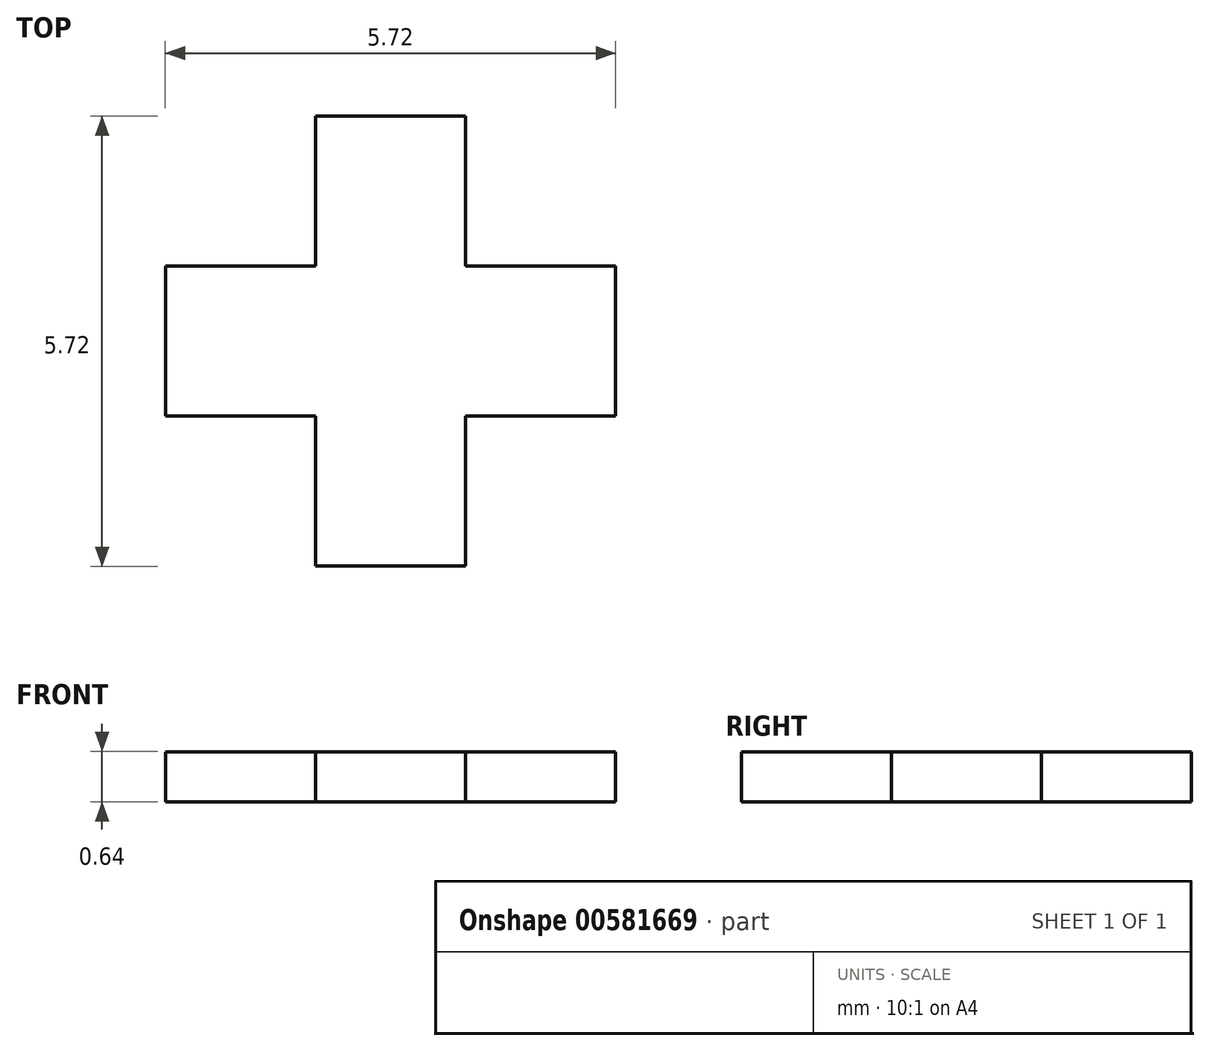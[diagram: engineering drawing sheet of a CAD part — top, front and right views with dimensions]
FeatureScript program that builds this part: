
annotation { "Feature Type Name" : "Feature", "Feature Type Description" : "" }
export const myFeature = defineFeature(function(context is Context, id is Id, definition is map)
    precondition{}
    {
        {
            var Q0;
            Q0=qCreatedBy(makeId("Top.planeOp"),FACE);
            var sketch = newSketch(context, id + "F0", { "sketchPlane" : qUnion([Q0])});
            skLineSegment(sketch, "E0", {"start": v(-33.75, -11.5) * mm, "end": v(-35.65, -11.5) * mm});
            skLineSegment(sketch, "E1", {"start": v(-35.65, -11.5) * mm, "end": v(-35.65, -13.4) * mm});
            skLineSegment(sketch, "E2", {"start": v(-35.65, -13.4) * mm, "end": v(-37.56, -13.4) * mm});
            skLineSegment(sketch, "E3", {"start": v(-37.56, -13.4) * mm, "end": v(-37.56, -15.3) * mm});
            skLineSegment(sketch, "E4", {"start": v(-37.56, -15.3) * mm, "end": v(-35.65, -15.3) * mm});
            skLineSegment(sketch, "E5", {"start": v(-35.65, -15.3) * mm, "end": v(-35.65, -17.2) * mm});
            skLineSegment(sketch, "E6", {"start": v(-35.65, -17.2) * mm, "end": v(-33.75, -17.2) * mm});
            skLineSegment(sketch, "E7", {"start": v(-33.75, -17.2) * mm, "end": v(-33.75, -15.3) * mm});
            skLineSegment(sketch, "E8", {"start": v(-33.75, -15.3) * mm, "end": v(-31.84, -15.3) * mm});
            skLineSegment(sketch, "E9", {"start": v(-31.84, -15.3) * mm, "end": v(-31.84, -13.4) * mm});
            skLineSegment(sketch, "E10", {"start": v(-31.84, -13.4) * mm, "end": v(-33.75, -13.4) * mm});
            skLineSegment(sketch, "E11", {"start": v(-33.75, -13.4) * mm, "end": v(-33.75, -11.5) * mm});
            skSolve(sketch);
        }
        {
            var Q0;
            Q0 = qSketchRegion(id + "F0", true);
            extrude(context, id + "F1", {"entities" : qUnion([Q0]), "depth" : 0.64 * mm, "offsetDistance" : 25.4 * mm});
        }
    });
